# Revit family: F089-38x38x32
name_source: partatom
category: Furniture
units: mm (PartAtom-declared; Revit-internal decimal feet)

## family parameters
Always vertical = Yes
Cut with Voids When Loaded = No
OmniClass Number = 23.40.20.00
OmniClass Title = General Furniture and Specialties
Room Calculation Point = No
Shared = No
Work Plane-Based = No

## types (2) — shared parameters
Back Fabric = <By Category>
Base Finish = <By Category>
Glide = <By Category>
Low Emitting Finish = Yes
Low Emitting Material = Yes
Low Profile = Black
Manufacturer = Fomcore
Product Documentation Link = https://fomcore.com
Salvage or Reuse = Yes
Side Fabric = <By Category>
Step 1 Fabric = <By Category>
Step 2 Fabric = <By Category>
Step 3 Fabric = <By Category>
Type Comments = Step Series
URL = https://fomcore.com
zero-valued in all types: Cost, Percentage of Recycled Content

## per-type parameters (varying)
| type | BH | Description | G1 | L1 |
| F089-38x38x32-G1 | 3/4" | Three Step Inside Curved Corner, 38Lx38Wx32H, Glide | Yes | No |
| F089-38x38x32-L1 | 1/2" | Three Step Inside Curved Corner, 38Lx38Wx32H, Low Profie | No | Yes |

note: column(s) folded — value = type name in every type: Model

## geometry (parser evidence)
native form markers: Sweep x2
no freeform markers — native parametric forms only
